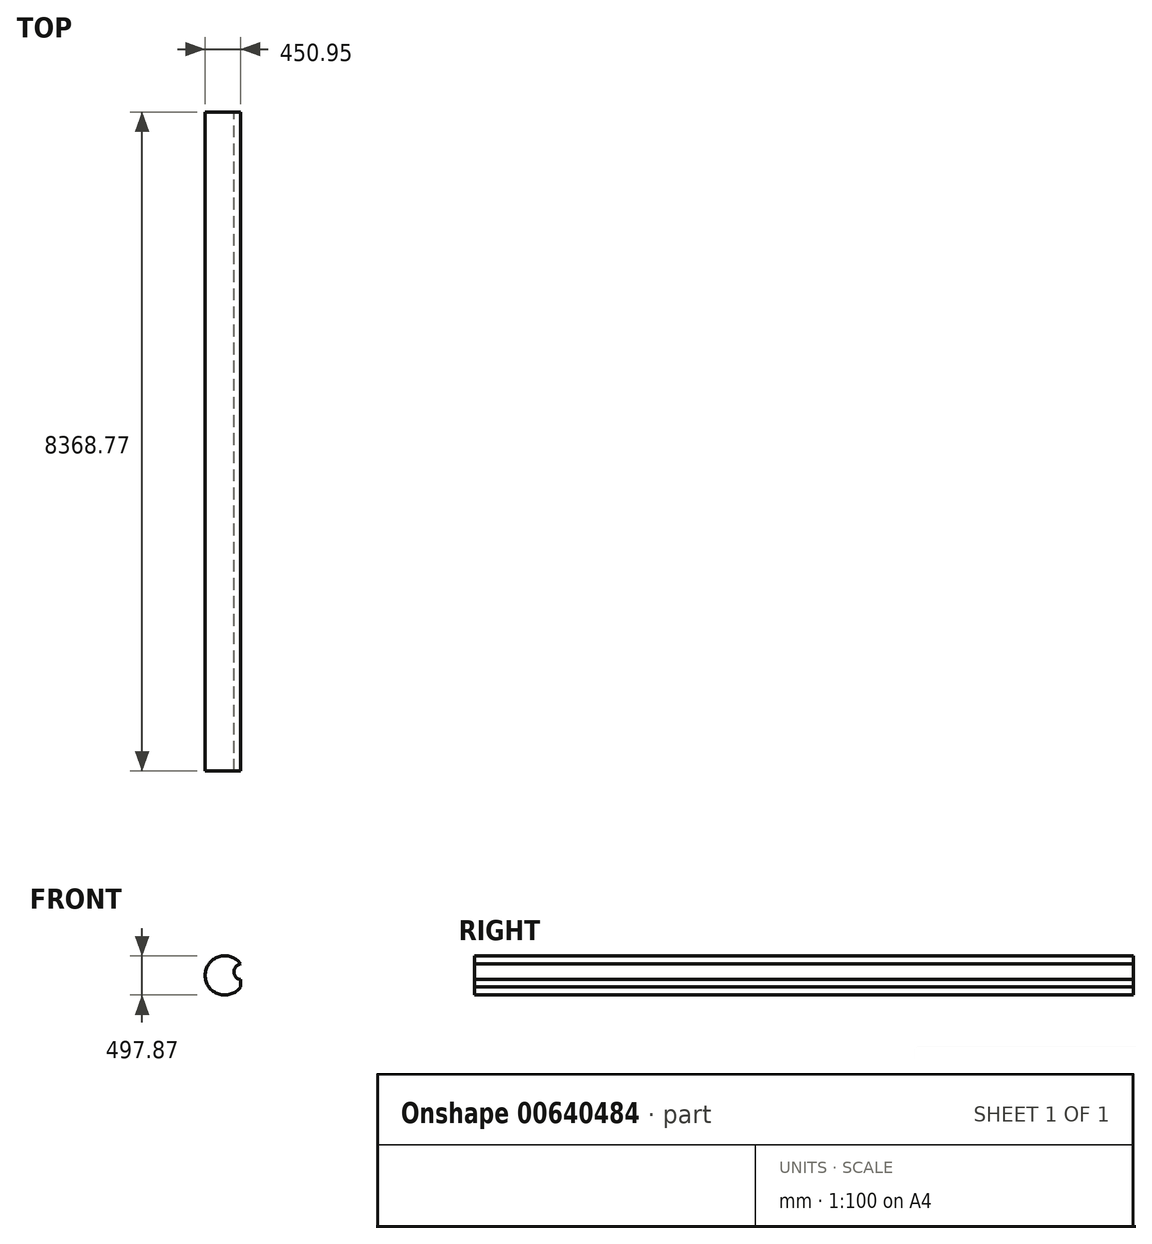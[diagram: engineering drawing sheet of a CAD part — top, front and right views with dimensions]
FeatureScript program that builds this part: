
annotation { "Feature Type Name" : "Feature", "Feature Type Description" : "" }
export const myFeature = defineFeature(function(context is Context, id is Id, definition is map)
    precondition{}
    {
        {
            var Q0;
            Q0=qCreatedBy(makeId("Front.planeOp"),FACE);
            var sketch = newSketch(context, id + "F0", { "sketchPlane" : qUnion([Q0])});
            skArc(sketch, "E0", {"start": v(32.44, 32.75) * mm, "mid": v(-141.34, 128.61) * mm, "end": v(0, -10.72) * mm});
            skArc(sketch, "E1", {"start": v(-29.28, 32.97) * mm, "mid": v(-526.13, 42.13) * mm, "end": v(-34.14, -27.8) * mm});
            skArc(sketch, "E2", {"start": v(-68.92, 140.94) * mm, "mid": v(5368.59, -331.06) * mm, "end": v(-59.42, 239.9) * mm});
            skSolve(sketch);
        }
        {
            var Q0;
            {var subQ0=sQuery(id+"F0.wireOp",EDGE,"E1");var subQ1=sQuery(id+"F0.wireOp",EDGE,"E0");var subQ2=makeQuery(id+"F0.imprint","INTERSECT",VERTEX,{"disambiguationData":[OD(1.0)],"derivedFrom":[subQ1,subQ0]});Q0=makeQuery(id+"F0.imprint","IMPRINT",FACE,{"disambiguationData":[TD([[makeQuery(id+"F0.imprint","IMPRINT",EDGE,{"disambiguationData":[TD([[subQ2,-1.0]])],"derivedFrom":subQ1}),-1.0]])]});}
            extrude(context, id + "F1", {"entities" : qUnion([Q0]), "depth" : 8368.77 * mm, "offsetDistance" : 25.4 * mm});
        }
    });
